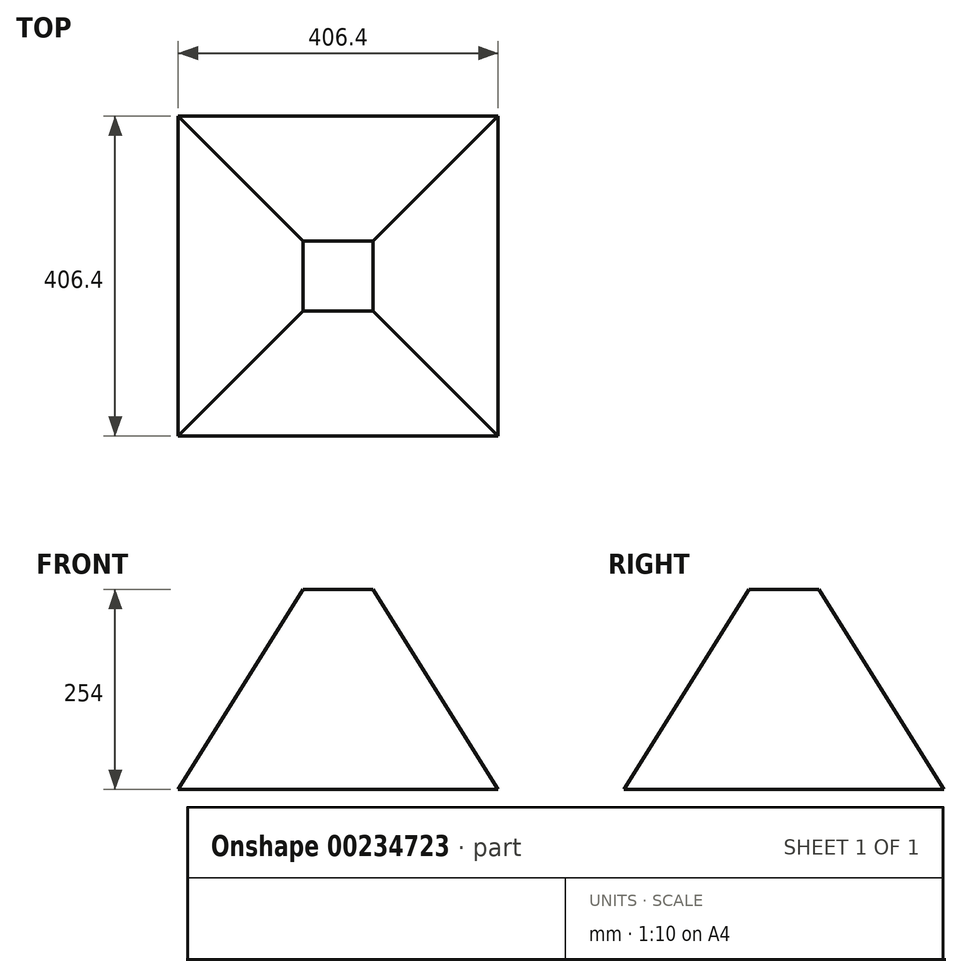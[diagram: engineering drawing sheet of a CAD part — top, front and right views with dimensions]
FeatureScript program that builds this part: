
annotation { "Feature Type Name" : "Feature", "Feature Type Description" : "" }
export const myFeature = defineFeature(function(context is Context, id is Id, definition is map)
    precondition{}
    {
        {
            var Q0;
            Q0=qCreatedBy(makeId("Top.planeOp"),FACE);
            var sketch = newSketch(context, id + "F0", { "sketchPlane" : qUnion([Q0])});
            skLineSegment(sketch, "E0.bottom", {"start": v(-46.18, 361.45) * mm, "end": v(360.22, 361.45) * mm});
            skLineSegment(sketch, "E0.top", {"start": v(-46.18, -44.95) * mm, "end": v(360.22, -44.95) * mm});
            skLineSegment(sketch, "E0.left", {"start": v(-46.18, 361.45) * mm, "end": v(-46.18, -44.95) * mm});
            skLineSegment(sketch, "E0.right", {"start": v(360.22, 361.45) * mm, "end": v(360.22, -44.95) * mm});
            skSolve(sketch);
        }
        {
            var Q0;
            Q0=makeQuery(id+"F0.imprint","IMPRINT",FACE,{"disambiguationData":[TD([[makeQuery(id+"F0.imprint","IMPRINT",EDGE,{"derivedFrom":sQuery(id+"F0.wireOp",EDGE,"E0.bottom")}),-1.0]])]});
            extrude(context, id + "F1", {"entities" : qUnion([Q0]), "depth" : 254 * mm});
        }
        {
            var Q0;
            Q0=makeQuery(id+"F1.opExtrude","CAP_EDGE",EDGE,{"disambiguationData":[OSD([sQuery(id+"F0.wireOp",EDGE,"E0.left")])],"isStart":false});
            var Q1;
            Q1=makeQuery(id+"F1.opExtrude","CAP_EDGE",EDGE,{"disambiguationData":[OSD([sQuery(id+"F0.wireOp",EDGE,"E0.bottom")])],"isStart":false});
            var Q2;
            Q2=makeQuery(id+"F1.opExtrude","CAP_EDGE",EDGE,{"disambiguationData":[OSD([sQuery(id+"F0.wireOp",EDGE,"E0.right")])],"isStart":false});
            var Q3;
            Q3=makeQuery(id+"F1.opExtrude","CAP_EDGE",EDGE,{"disambiguationData":[OSD([sQuery(id+"F0.wireOp",EDGE,"E0.top")])],"isStart":false});
            chamfer(context, id + "F2", {"entities" : qUnion([Q0, Q1, Q2, Q3]), "chamferType" : ChamferType.OFFSET_ANGLE, "width" : 158.75 * mm, "oppositeDirection" : false, "angle" : 58 * degree, "tangentPropagation" : true});
        }
    });
